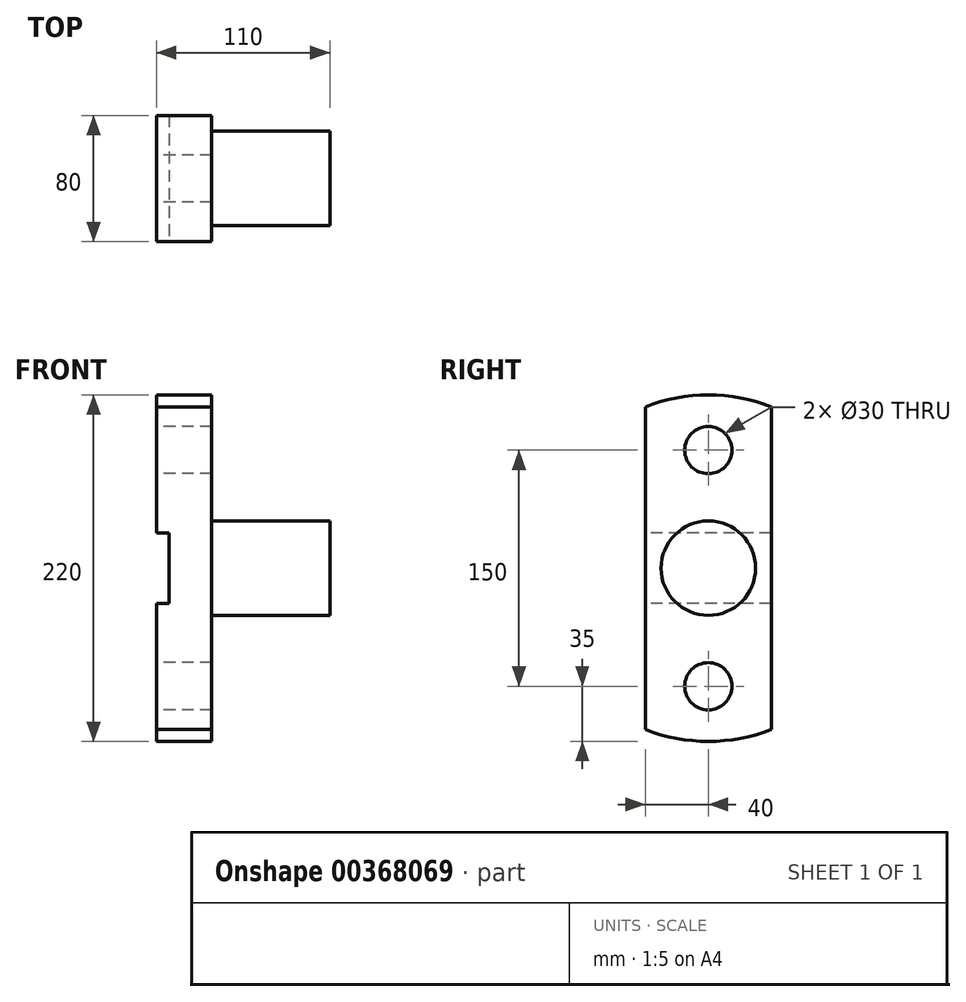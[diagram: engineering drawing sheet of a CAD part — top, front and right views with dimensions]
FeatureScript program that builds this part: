
annotation { "Feature Type Name" : "Feature", "Feature Type Description" : "" }
export const myFeature = defineFeature(function(context is Context, id is Id, definition is map)
    precondition{}
    {
        {
            var Q0;
            Q0=qCreatedBy(makeId("Right.planeOp"),FACE);
            var sketch = newSketch(context, id + "F0", { "sketchPlane" : qUnion([Q0])});
            skArc(sketch, "E0", {"start": v(-40, -102.47) * mm, "mid": v(0, -110) * mm, "end": v(40, -102.47) * mm});
            skLineSegment(sketch, "E1", {"start": v(-40, 102.47) * mm, "end": v(-40, -102.47) * mm});
            skLineSegment(sketch, "E2", {"start": v(40, 102.47) * mm, "end": v(40, -102.47) * mm});
            skArc(sketch, "E3.trimOffspring", {"start": v(40, 102.47) * mm, "mid": v(0, 110) * mm, "end": v(-40, 102.47) * mm});
            skCircle(sketch, "E4", {"center": v(0, 75) * mm, "radius": 15 * mm});
            skCircle(sketch, "E5", {"center": v(0, -75) * mm, "radius": 15 * mm});
            skSolve(sketch);
        }
        {
            var Q0;
            Q0=makeQuery(id+"F0.imprint","IMPRINT",FACE,{"disambiguationData":[TD([[makeQuery(id+"F0.imprint","IMPRINT",EDGE,{"derivedFrom":sQuery(id+"F0.wireOp",EDGE,"E0")}),1.0]])]});
            extrude(context, id + "F1", {"entities" : qUnion([Q0]), "depth" : 35 * mm});
        }
        {
            var Q0;
            Q0=makeQuery(id+"F1.opExtrude","CAP_FACE",FACE,{"disambiguationData":[OSD([sQuery(id+"F0.wireOp",EDGE,"E0"),sQuery(id+"F0.wireOp",EDGE,"E1"),sQuery(id+"F0.wireOp",EDGE,"E2"),sQuery(id+"F0.wireOp",EDGE,"E3.trimOffspring"),sQuery(id+"F0.wireOp",EDGE,"E4"),sQuery(id+"F0.wireOp",EDGE,"E5")])],"isStart":false});
            var sketch = newSketch(context, id + "F2", { "sketchPlane" : qUnion([Q0])});
            skCircle(sketch, "E6", {"center": v(0, 0) * mm, "radius": 30 * mm});
            skSolve(sketch);
        }
        {
            var Q0;
            Q0=makeQuery(id+"F2.imprint","IMPRINT",FACE,{"disambiguationData":[TD([[makeQuery(id+"F2.imprint","IMPRINT",EDGE,{"derivedFrom":sQuery(id+"F2.wireOp",EDGE,"E6")}),1.0]])]});
            extrude(context, id + "F3", {"entities" : qUnion([Q0]), "operationType" : NewBodyOperationType.ADD, "depth" : 75 * mm});
        }
        {
            var Q0;
            Q0=qCreatedBy(makeId("Front.planeOp"),FACE);
            var sketch = newSketch(context, id + "F4", { "sketchPlane" : qUnion([Q0])});
            skLineSegment(sketch, "E7.bottom", {"start": v(0, 22.5) * mm, "end": v(8, 22.5) * mm});
            skLineSegment(sketch, "E7.top", {"start": v(0, -22.5) * mm, "end": v(8, -22.5) * mm});
            skLineSegment(sketch, "E7.left", {"start": v(0, 22.5) * mm, "end": v(0, -22.5) * mm});
            skLineSegment(sketch, "E7.right", {"start": v(8, 22.5) * mm, "end": v(8, -22.5) * mm});
            skSolve(sketch);
        }
        {
            var Q0;
            Q0=qSketchRegion(id+"F4",true);
            extrude(context, id + "F5", {"entities" : qUnion([Q0]), "operationType" : NewBodyOperationType.REMOVE, "endBound" : BoundingType.THROUGH_ALL, "oppositeDirection" : true, "depth" : 25 * mm, "hasSecondDirection" : true, "secondDirectionBound" : SecondDirectionBoundingType.THROUGH_ALL, "secondDirectionOppositeDirection" : false, "secondDirectionDepth" : 25 * mm});
        }
    });
